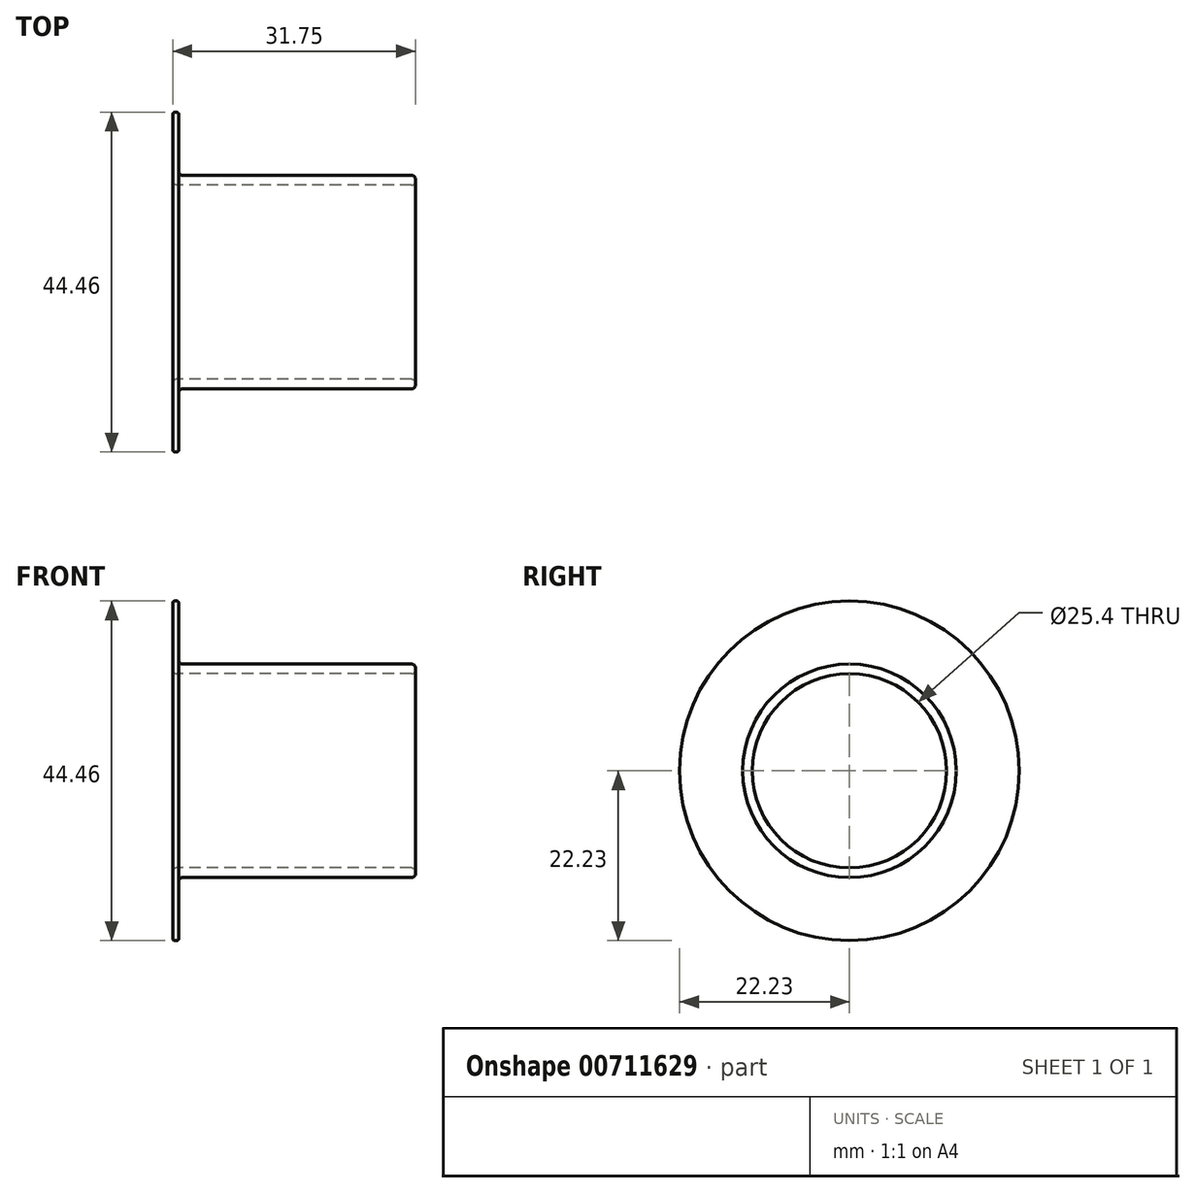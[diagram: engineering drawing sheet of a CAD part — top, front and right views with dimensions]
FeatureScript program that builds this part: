
annotation { "Feature Type Name" : "Feature", "Feature Type Description" : "" }
export const myFeature = defineFeature(function(context is Context, id is Id, definition is map)
    precondition{}
    {
        {
            var Q0;
            Q0=qCreatedBy(makeId("Top.planeOp"),FACE);
            var sketch = newSketch(context, id + "F0", { "sketchPlane" : qUnion([Q0])});
            skLineSegment(sketch, "E0", {"start": v(31.75, 13.2) * mm, "end": v(31.75, 13.46) * mm});
            skLineSegment(sketch, "E1", {"start": v(31.24, 13.97) * mm, "end": v(1.27, 13.97) * mm});
            skLineSegment(sketch, "E2", {"start": v(0, 13.2) * mm, "end": v(0, 21.97) * mm});
            skLineSegment(sketch, "E3", {"start": v(0.25, 22.22) * mm, "end": v(0.5, 22.22) * mm});
            skLineSegment(sketch, "E4", {"start": v(0.76, 21.97) * mm, "end": v(0.76, 14.48) * mm});
            skLineSegment(sketch, "E5.0", {"start": v(31.24, 12.7) * mm, "end": v(0.5, 12.7) * mm});
            skLineSegment(sketch, "E6", {"start": v(-9.54, 0) * mm, "end": v(41.06, 0) * mm, "construction": true});
            skPoint(sketch, "E7.visualSharp", {"position": v(0.76, 13.97) * mm});
            skArc(sketch, "E7.filletArc", {"start": v(0.76, 14.48) * mm, "mid": v(0.91, 14.12) * mm, "end": v(1.27, 13.97) * mm});
            skPoint(sketch, "E8.visualSharp", {"position": v(0, 12.7) * mm});
            skArc(sketch, "E8.filletArc", {"start": v(0, 13.2) * mm, "mid": v(0.15, 12.85) * mm, "end": v(0.5, 12.7) * mm});
            skPoint(sketch, "E9.visualSharp", {"position": v(31.75, 12.7) * mm});
            skArc(sketch, "E9.filletArc", {"start": v(31.24, 12.7) * mm, "mid": v(31.6, 12.85) * mm, "end": v(31.75, 13.2) * mm});
            skPoint(sketch, "E10.visualSharp", {"position": v(31.75, 13.97) * mm});
            skArc(sketch, "E10.filletArc", {"start": v(31.75, 13.46) * mm, "mid": v(31.6, 13.82) * mm, "end": v(31.24, 13.97) * mm});
            skPoint(sketch, "E11.visualSharp", {"position": v(0, 22.22) * mm});
            skArc(sketch, "E11.filletArc", {"start": v(0.25, 22.22) * mm, "mid": v(0.07, 22.15) * mm, "end": v(0, 21.97) * mm});
            skPoint(sketch, "E12.visualSharp", {"position": v(0.76, 22.22) * mm});
            skArc(sketch, "E12.filletArc", {"start": v(0.76, 21.97) * mm, "mid": v(0.69, 22.15) * mm, "end": v(0.5, 22.23) * mm});
            skSolve(sketch);
        }
        {
            var Q0;
            Q0 = qSketchRegion(id + "F0", true);
            var Q1;
            Q1=sQuery(id+"F0.wireOp",EDGE,"E6");
            revolve(context, id + "F1", {"surfaceOperationType" : NewSurfaceOperationType.NEW, "entities" : qUnion([Q0]), "axis" : qUnion([Q1]), "revolveType" : RevolveType.FULL});
        }
    });
